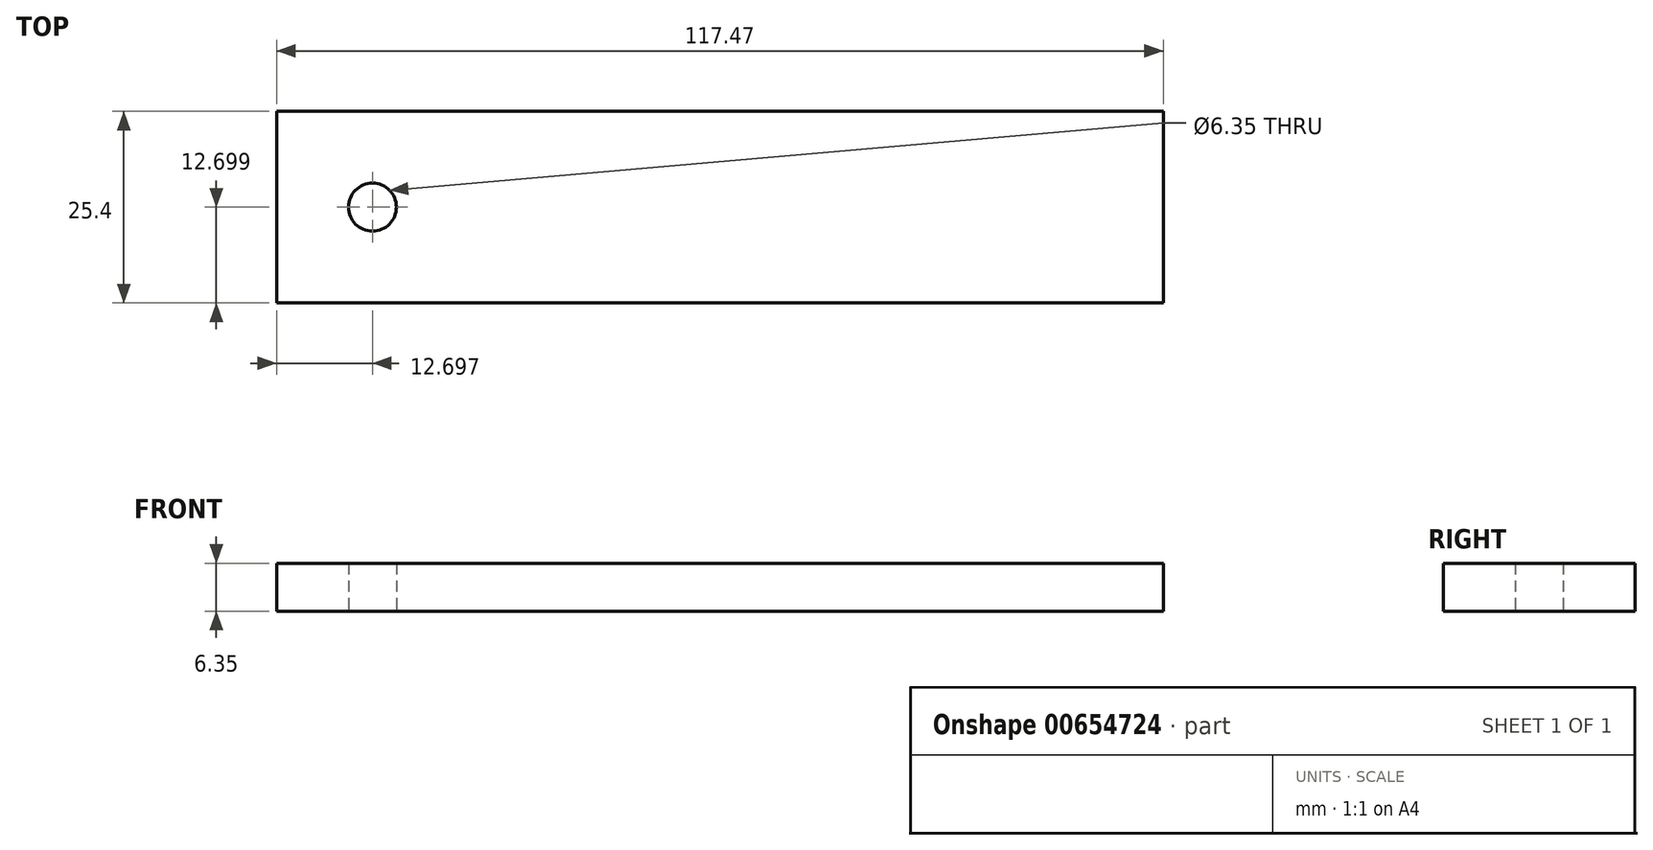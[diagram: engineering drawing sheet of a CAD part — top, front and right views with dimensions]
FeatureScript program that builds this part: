
annotation { "Feature Type Name" : "Feature", "Feature Type Description" : "" }
export const myFeature = defineFeature(function(context is Context, id is Id, definition is map)
    precondition{}
    {
        {
            var Q0;
            Q0=qCreatedBy(makeId("Top.planeOp"),FACE);
            var sketch = newSketch(context, id + "F0", { "sketchPlane" : qUnion([Q0])});
            skLineSegment(sketch, "E0.bottom", {"start": v(-60.84, 5.92) * mm, "end": v(56.63, 5.92) * mm});
            skLineSegment(sketch, "E0.top", {"start": v(-60.84, -19.48) * mm, "end": v(56.63, -19.48) * mm});
            skLineSegment(sketch, "E0.left", {"start": v(-60.84, 5.92) * mm, "end": v(-60.84, -19.48) * mm});
            skLineSegment(sketch, "E0.right", {"start": v(56.63, 5.92) * mm, "end": v(56.63, -19.48) * mm});
            skCircle(sketch, "E1", {"center": v(-48.14, -6.78) * mm, "radius": 3.18 * mm});
            skSolve(sketch);
        }
        {
            var Q0;
            Q0 = qSketchRegion(id + "F0", true);
            extrude(context, id + "F1", {"entities" : qUnion([Q0]), "depth" : 6.35 * mm, "offsetDistance" : 25.4 * mm});
        }
    });
